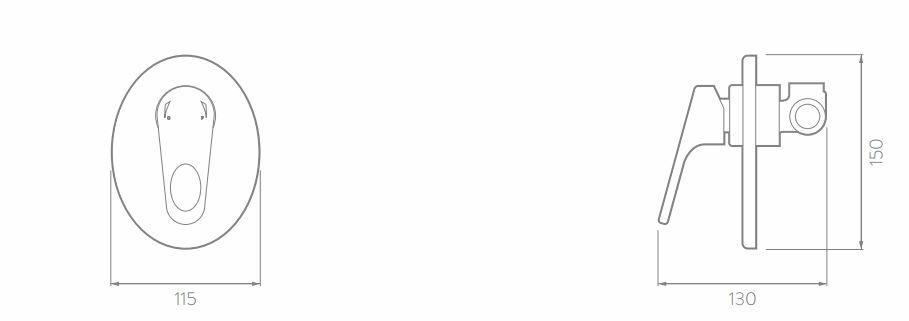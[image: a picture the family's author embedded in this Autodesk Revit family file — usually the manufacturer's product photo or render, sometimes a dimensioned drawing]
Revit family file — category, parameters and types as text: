
# Revit family: KR4095551_Mezclador Ducha Monocontrol Koral SSB
name_source: partatom
category: Plumbing Fixtures
units: mm (PartAtom-declared; Revit-internal decimal feet)

## family parameters
Always vertical = Yes
Cut with Voids When Loaded = No
Host = Wall
OmniClass Number = 23.31.11.00
OmniClass Title = Faucets
Part Type = Normal
Room Calculation Point = No
Round Connector Dimension = Use Diameter
Shared = No

## types (1)
- Type 1
    Alto = 946 mm
    Altura ducha = 2000 mm  [stored 6.56168 ft]
    Altura mezclador = 1200 mm
    Ancho = 152 mm
    Capacidad de flujo = 80 psi: 9,3 L/min
    Creado por = IDD
    Fabricante = Corona
    Fecha de creación = 09/10/2020
    Garantía = 30 años
    Material = Corona_Niquel
    Peso neto = 1.200 g. - 2,60 lb
    Presion maxima = 125 psi (860 kPa)
    Presion minima = 20 psi (140 kPa)
    Profundidad = 329 mm  [stored 1.0794 ft]
    Referencia = KR4095551
    Temperatura de uso = 5˚C a 71˚C
    URL = https://corona.co

note: [stored X ft] marks values corroborated as IEEE doubles in the binary element streams (Revit-internal decimal feet)

## geometry (parser evidence)
native form markers: Sweep x9
no freeform markers — native parametric forms only
